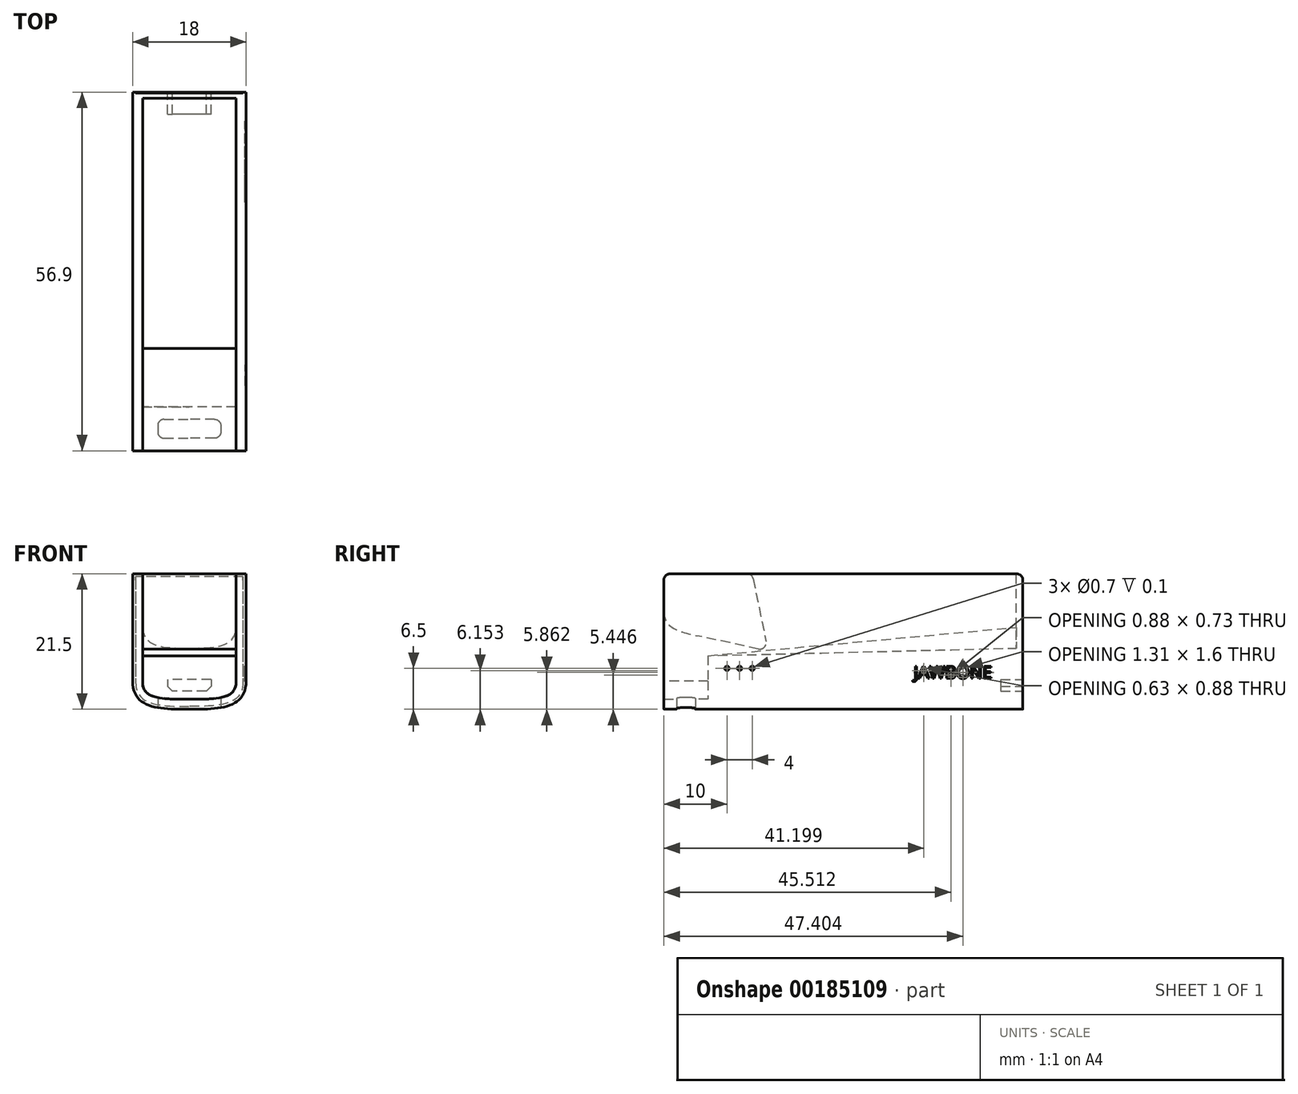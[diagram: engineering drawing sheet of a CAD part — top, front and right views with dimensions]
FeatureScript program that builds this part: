
annotation { "Feature Type Name" : "Feature", "Feature Type Description" : "" }
export const myFeature = defineFeature(function(context is Context, id is Id, definition is map)
    precondition{}
    {
        {
            var Q0;
            Q0=qCreatedBy(makeId("Front.planeOp"),FACE);
            var sketch = newSketch(context, id + "F0", { "sketchPlane" : qUnion([Q0])});
            skLineSegment(sketch, "E0", {"start": v(0, 21.5) * mm, "end": v(-9, 21.5) * mm});
            skLineSegment(sketch, "E1", {"start": v(-9, 21.5) * mm, "end": v(-9, 4.5) * mm});
            skFitSpline(sketch, "E2", {"points": [v(-9, 4.5) * mm, v(0, 0) * mm], "startDerivative": vector(0, -13.5) * mm, "endDerivative": vector(13.5, 0) * mm});
            skLineSegment(sketch, "E3", {"start": v(0, 21.5) * mm, "end": v(0, 0) * mm, "construction": true});
            skLineSegment(sketch, "E4.MirrorCS", {"start": v(0, 21.5) * mm, "end": v(9, 21.5) * mm});
            skLineSegment(sketch, "E5.MirrorCS", {"start": v(9, 21.5) * mm, "end": v(9, 4.5) * mm});
            skFitSpline(sketch, "E6.MirrorCS", {"points": [v(9, 4.5) * mm, v(0, 0) * mm], "startDerivative": vector(0, -13.5) * mm, "endDerivative": vector(-13.5, 0) * mm});
            skLineSegment(sketch, "E7", {"start": v(-9, 4.5) * mm, "end": v(-9, 0) * mm, "construction": true});
            skLineSegment(sketch, "E8", {"start": v(-9, 0) * mm, "end": v(-4.5, 0) * mm, "construction": true});
            skLineSegment(sketch, "E9", {"start": v(-4.5, 0) * mm, "end": v(0, 0) * mm, "construction": true});
            skSolve(sketch);
        }
        {
            var Q0;
            Q0=makeQuery(id+"F0.imprint","IMPRINT",FACE,{"disambiguationData":[TD([[makeQuery(id+"F0.imprint","IMPRINT",EDGE,{"derivedFrom":sQuery(id+"F0.wireOp",EDGE,"E0")}),1.0]])]});
            extrude(context, id + "F1", {"entities" : qUnion([Q0]), "depth" : 56.9 * mm});
        }
        {
            var Q0;
            Q0=makeQuery(id+"F1.opExtrude","SWEPT_BODY",BODY,{"disambiguationData":[OSD([sQuery(id+"F0.wireOp",EDGE,"E0"),sQuery(id+"F0.wireOp",EDGE,"E1"),sQuery(id+"F0.wireOp",EDGE,"E2"),sQuery(id+"F0.wireOp",EDGE,"E4.MirrorCS"),sQuery(id+"F0.wireOp",EDGE,"E5.MirrorCS"),sQuery(id+"F0.wireOp",EDGE,"E6.MirrorCS")])]});
            var Q1;
            Q1=sQuery(id+"F0.wireOp",EDGE,"E3");
            transform(context, id + "F2", {"entities" : qUnion([Q0]), "transformType" : TransformType.ROTATION, "transformAxis" : qUnion([Q1]), "angle" : 180 * degree, "makeCopy" : false});
        }
        {
            var Q0;
            Q0=makeQuery(id+"F1.opExtrude","CAP_FACE",FACE,{"disambiguationData":[OSD([sQuery(id+"F0.wireOp",EDGE,"E0"),sQuery(id+"F0.wireOp",EDGE,"E1"),sQuery(id+"F0.wireOp",EDGE,"E2"),sQuery(id+"F0.wireOp",EDGE,"E4.MirrorCS"),sQuery(id+"F0.wireOp",EDGE,"E5.MirrorCS"),sQuery(id+"F0.wireOp",EDGE,"E6.MirrorCS")])],"isStart":false});
            cPlane(context, id + "F3", {"entities" : qUnion([Q0]), "cplaneType" : CPlaneType.OFFSET, "offset" : 0 * mm, "width" : 150 * mm, "height" : 150 * mm});
        }
        {
            var Q0;
            Q0=qCreatedBy(id+"F3.planeOp",FACE);
            var sketch = newSketch(context, id + "F4", { "sketchPlane" : qUnion([Q0])});
            skLineSegment(sketch, "E10.0", {"start": v(8.5, 21.5) * mm, "end": v(8.5, 4.5) * mm});
            skFitSpline(sketch, "E10.1", {"points": [v(8.5, 4.5) * mm, v(8.5, 3.98) * mm, v(8.37, 3.1) * mm, v(7.88, 2.16) * mm, v(7.12, 1.49) * mm, v(6.07, 1) * mm, v(4.78, 0.7) * mm, v(2.8, 0.5) * mm, v(1.13, 0.5) * mm, v(0, 0.5) * mm]});
            skFitSpline(sketch, "E10.2", {"points": [v(-8.5, 4.5) * mm, v(-8.5, 3.98) * mm, v(-8.37, 3.1) * mm, v(-7.88, 2.16) * mm, v(-7.12, 1.49) * mm, v(-6.07, 1) * mm, v(-4.78, 0.7) * mm, v(-2.8, 0.5) * mm, v(-1.13, 0.5) * mm, v(0, 0.5) * mm]});
            skLineSegment(sketch, "E10.3", {"start": v(-8.5, 21.5) * mm, "end": v(-8.5, 4.5) * mm});
            skLineSegment(sketch, "E11", {"start": v(-8.5, 21.5) * mm, "end": v(8.5, 21.5) * mm});
            skSolve(sketch);
        }
        {
            var Q0;
            Q0 = qSketchRegion(id + "F4", true);
            extrude(context, id + "F5", {"entities" : qUnion([Q0]), "operationType" : NewBodyOperationType.REMOVE, "oppositeDirection" : true, "depth" : 0.15 * mm});
        }
        {
            var Q0;
            Q0=makeQuery(id+"F1.opExtrude","CAP_EDGE",EDGE,{"disambiguationData":[OSD([sQuery(id+"F0.wireOp",EDGE,"E0"),sQuery(id+"F0.wireOp",EDGE,"E4.MirrorCS")])],"isStart":false});
            var Q1;
            Q1=makeQuery(id+"F1.opExtrude","CAP_EDGE",EDGE,{"disambiguationData":[OSD([sQuery(id+"F0.wireOp",EDGE,"E0"),sQuery(id+"F0.wireOp",EDGE,"E4.MirrorCS")])],"isStart":true});
            fillet(context, id + "F6", {"entities" : qUnion([Q0, Q1]), "radius" : 1 * mm, "allowEdgeOverflow" : false});
        }
        {
            var Q0;
            Q0=makeQuery(id+"F1.opExtrude","CAP_FACE",FACE,{"disambiguationData":[OSD([sQuery(id+"F0.wireOp",EDGE,"E0"),sQuery(id+"F0.wireOp",EDGE,"E1"),sQuery(id+"F0.wireOp",EDGE,"E2"),sQuery(id+"F0.wireOp",EDGE,"E4.MirrorCS"),sQuery(id+"F0.wireOp",EDGE,"E5.MirrorCS"),sQuery(id+"F0.wireOp",EDGE,"E6.MirrorCS")])],"isStart":false});
            cPlane(context, id + "F7", {"entities" : qUnion([Q0]), "cplaneType" : CPlaneType.OFFSET, "offset" : 0 * mm, "width" : 150 * mm, "height" : 150 * mm});
        }
        {
            var Q0;
            Q0=qCreatedBy(id+"F7.planeOp",FACE);
            var sketch = newSketch(context, id + "F8", { "sketchPlane" : qUnion([Q0])});
            skLineSegment(sketch, "E12", {"start": v(0, 4.75) * mm, "end": v(-3.45, 4.75) * mm});
            skLineSegment(sketch, "E13", {"start": v(-3.45, 4.75) * mm, "end": v(-3.45, 3.65) * mm});
            skLineSegment(sketch, "E14", {"start": v(-3.45, 3.65) * mm, "end": v(-2.7, 2.9) * mm});
            skLineSegment(sketch, "E15", {"start": v(-2.7, 2.9) * mm, "end": v(0, 2.9) * mm});
            skLineSegment(sketch, "E16.MirrorCS", {"start": v(0, 4.75) * mm, "end": v(3.45, 4.75) * mm});
            skLineSegment(sketch, "E17.MirrorCS", {"start": v(3.45, 4.75) * mm, "end": v(3.45, 3.65) * mm});
            skLineSegment(sketch, "E18.MirrorCS", {"start": v(3.45, 3.65) * mm, "end": v(2.7, 2.9) * mm});
            skLineSegment(sketch, "E19.MirrorCS", {"start": v(2.7, 2.9) * mm, "end": v(0, 2.9) * mm});
            skSolve(sketch);
        }
        {
            var Q0;
            Q0 = qSketchRegion(id + "F8", true);
            extrude(context, id + "F9", {"entities" : qUnion([Q0]), "operationType" : NewBodyOperationType.REMOVE, "oppositeDirection" : true, "depth" : 3.5 * mm});
        }
        {
            var Q0;
            Q0=qCreatedBy(makeId("Front.planeOp"),FACE);
            var sketch = newSketch(context, id + "F10", { "sketchPlane" : qUnion([Q0])});
            skLineSegment(sketch, "E20.0", {"start": v(-7.4, 21.5) * mm, "end": v(-7.4, 4.5) * mm});
            skFitSpline(sketch, "E20.1", {"points": [v(-7.4, 4.5) * mm, v(-7.4, 4.07) * mm, v(-7.32, 3.57) * mm, v(-7.14, 3.13) * mm, v(-6.97, 2.87) * mm, v(-6.76, 2.65) * mm, v(-6.4, 2.37) * mm, v(-5.74, 2.06) * mm, v(-4.6, 1.8) * mm, v(-3.23, 1.65) * mm, v(-1.67, 1.6) * mm, v(-0.56, 1.6) * mm, v(0, 1.6) * mm]});
            skFitSpline(sketch, "E20.2", {"points": [v(7.4, 4.5) * mm, v(7.4, 4.07) * mm, v(7.32, 3.57) * mm, v(7.14, 3.13) * mm, v(6.97, 2.87) * mm, v(6.76, 2.65) * mm, v(6.4, 2.37) * mm, v(5.74, 2.06) * mm, v(4.6, 1.8) * mm, v(3.23, 1.65) * mm, v(1.67, 1.6) * mm, v(0.56, 1.6) * mm, v(0, 1.6) * mm]});
            skLineSegment(sketch, "E20.3", {"start": v(7.4, 21.5) * mm, "end": v(7.4, 4.5) * mm});
            skLineSegment(sketch, "E21", {"start": v(7.4, 21.5) * mm, "end": v(-7.4, 21.5) * mm});
            skSolve(sketch);
        }
        {
            var Q0;
            {var subQ1=sQuery(id+"F10.wireOp",EDGE,"E20.1");Q0=makeQuery(id+"F10.imprint","IMPRINT",FACE,{"disambiguationData":[TD([[makeQuery(id+"F10.imprint","IMPRINT",EDGE,{"derivedFrom":subQ1}),1.0]])]});}
            var Q1;
            {var subQ0=sQuery(id+"F10.wireOp",EDGE,"E21");Q1=makeQuery(id+"F10.imprint","IMPRINT",FACE,{"disambiguationData":[TD([[makeQuery(id+"F10.imprint","IMPRINT",EDGE,{"derivedFrom":subQ0}),1.0]])]});}
            extrude(context, id + "F11", {"entities" : qUnion([Q0, Q1]), "operationType" : NewBodyOperationType.REMOVE, "oppositeDirection" : true, "depth" : 7 * mm});
        }
        {
            var Q0;
            {var subQ0=sQuery(id+"F0.wireOp",EDGE,"E4.MirrorCS");var subQ1=sQuery(id+"F0.wireOp",EDGE,"E0");Q0=makeQuery(id+"F6.opFillet","BLEND_EDGE",EDGE,{"blendedFrom":[makeQuery(id+"F1.opExtrude","CAP_EDGE",EDGE,{"disambiguationData":[OSD([subQ1,subQ0])],"isStart":false}),makeQuery(id+"F1.opExtrude","SWEPT_FACE",FACE,{"disambiguationData":[OSD([subQ1,subQ0])]})],"blendedInto":[makeQuery(id+"F1.opExtrude","SWEPT_FACE",FACE,{"disambiguationData":[OSD([subQ1,subQ0])]})]});}
            cPoint(context, id + "F12", {"entities" : qUnion([Q0]), "parameter" : 0.5});
        }
        {
            var Q0;
            Q0=makeQuery(id+"F1.opExtrude","CAP_FACE",FACE,{"disambiguationData":[OSD([sQuery(id+"F0.wireOp",EDGE,"E0"),sQuery(id+"F0.wireOp",EDGE,"E1"),sQuery(id+"F0.wireOp",EDGE,"E2"),sQuery(id+"F0.wireOp",EDGE,"E4.MirrorCS"),sQuery(id+"F0.wireOp",EDGE,"E5.MirrorCS"),sQuery(id+"F0.wireOp",EDGE,"E6.MirrorCS")])],"isStart":false});
            var Q1;
            Q1 = qCreatedBy(id + "F12" ,VERTEX);
            cPlane(context, id + "F13", {"entities" : qUnion([Q0, Q1]), "cplaneType" : CPlaneType.PLANE_POINT, "offset" : 25 * mm, "width" : 150 * mm, "height" : 150 * mm});
        }
        {
            var Q0;
            Q0=makeQuery(id+"F11.boolean.opBoolean","COPY",FACE,{"derivedFrom":makeQuery(id+"F11.opExtrude","CAP_FACE",FACE,{"disambiguationData":[OSD([sQuery(id+"F10.wireOp",EDGE,"E20.0"),sQuery(id+"F10.wireOp",EDGE,"E20.1"),sQuery(id+"F10.wireOp",EDGE,"E20.2"),sQuery(id+"F10.wireOp",EDGE,"E20.3"),sQuery(id+"F10.wireOp",EDGE,"E21")])],"isStart":false})});
            cPlane(context, id + "F14", {"entities" : qUnion([Q0]), "cplaneType" : CPlaneType.OFFSET, "offset" : 0 * mm, "width" : 150 * mm, "height" : 150 * mm});
        }
        {
            var Q0;
            Q0=qCreatedBy(id+"F14.planeOp",FACE);
            var sketch = newSketch(context, id + "F15", { "sketchPlane" : qUnion([Q0])});
            skLineSegment(sketch, "E22", {"start": v(-7.4, 21.5) * mm, "end": v(7.4, 21.5) * mm});
            skLineSegment(sketch, "E23", {"start": v(-7.4, 21.5) * mm, "end": v(-7.4, 8.5) * mm});
            skLineSegment(sketch, "E24", {"start": v(7.4, 8.5) * mm, "end": v(-7.4, 8.5) * mm});
            skLineSegment(sketch, "E25", {"start": v(7.4, 8.5) * mm, "end": v(7.4, 21.5) * mm});
            skSolve(sketch);
        }
        {
            var Q0;
            Q0=qCreatedBy(id+"F13.planeOp",FACE);
            var sketch = newSketch(context, id + "F16", { "sketchPlane" : qUnion([Q0])});
            skLineSegment(sketch, "E26", {"start": v(-7.4, 21.5) * mm, "end": v(7.4, 21.5) * mm});
            skLineSegment(sketch, "E27", {"start": v(-7.4, 21.5) * mm, "end": v(-7.4, 13) * mm});
            skLineSegment(sketch, "E28", {"start": v(7.4, 13) * mm, "end": v(7.4, 21.5) * mm});
            skFitSpline(sketch, "E29", {"points": [v(7.4, 13) * mm, v(0, 9.7) * mm, v(-7.4, 13) * mm], "startDerivative": vector(0, -19.8) * mm, "endDerivative": vector(0, 19.8) * mm});
            skLineSegment(sketch, "E30", {"start": v(7.4, 13) * mm, "end": v(7.4, 9.7) * mm, "construction": true});
            skLineSegment(sketch, "E31", {"start": v(-7.4, 9.7) * mm, "end": v(0, 9.7) * mm, "construction": true});
            skLineSegment(sketch, "E32", {"start": v(0, 9.7) * mm, "end": v(7.4, 9.7) * mm, "construction": true});
            skLineSegment(sketch, "E33", {"start": v(-7.4, 9.7) * mm, "end": v(-7.4, 13) * mm, "construction": true});
            skSolve(sketch);
        }
        {
            var Q1;
            Q1 = qSketchRegion(id + "F15", true);
            var Q2;
            Q2 = qSketchRegion(id + "F16", true);
            loft(context, id + "F17", {"operationType" : NewBodyOperationType.REMOVE, "sheetProfilesArray" : [{ "sheetProfileEntities" : qUnion([Q1]) }, { "sheetProfileEntities" : qUnion([Q2]) }]});
        }
        {
            var Q0;
            {var subQ0=sQuery(id+"F0.wireOp",EDGE,"E4.MirrorCS");var subQ1=sQuery(id+"F0.wireOp",EDGE,"E0");Q0=makeQuery(id+"F17.boolean.opBoolean","SPLIT",FACE,{"disambiguationData":[TD([makeQuery(id+"F1.opExtrude","SWEPT_FACE",FACE,{"disambiguationData":[OSD([sQuery(id+"F0.wireOp",EDGE,"E1")])]})])],"derivedFrom":makeQuery(id+"F1.opExtrude","SWEPT_FACE",FACE,{"disambiguationData":[OSD([subQ1,subQ0])]})});}
            var Q1;
            Q1=qCreatedBy(makeId("Origin.pointOp"),VERTEX);
            cPlane(context, id + "F18", {"entities" : qUnion([Q0, Q1]), "cplaneType" : CPlaneType.PLANE_POINT, "offset" : 25 * mm, "width" : 150 * mm, "height" : 150 * mm});
        }
        {
            var Q0;
            Q0=qCreatedBy(id+"F18.planeOp",FACE);
            var sketch = newSketch(context, id + "F19", { "sketchPlane" : qUnion([Q0])});
            skLineSegment(sketch, "E34.top", {"start": v(-10.72, 0) * mm, "end": v(11.6, 0) * mm, "construction": true});
            skLineSegment(sketch, "E35.0", {"start": v(-4, 2) * mm, "end": v(4, 2) * mm});
            skLineSegment(sketch, "E35.1", {"start": v(-5, 3) * mm, "end": v(-5, 4) * mm});
            skLineSegment(sketch, "E35.2", {"start": v(-4, 5) * mm, "end": v(4, 5) * mm});
            skLineSegment(sketch, "E35.3", {"start": v(5, 3) * mm, "end": v(5, 4) * mm});
            skPoint(sketch, "E36.visualSharp", {"position": v(-5, 2) * mm});
            skArc(sketch, "E36.filletArc", {"start": v(-5, 3) * mm, "mid": v(-4.7, 2.3) * mm, "end": v(-4, 2) * mm});
            skPoint(sketch, "E37.visualSharp", {"position": v(5, 2) * mm});
            skArc(sketch, "E37.filletArc", {"start": v(4, 2) * mm, "mid": v(4.7, 2.3) * mm, "end": v(5, 3) * mm});
            skPoint(sketch, "E38.visualSharp", {"position": v(5, 5) * mm});
            skArc(sketch, "E38.filletArc", {"start": v(5, 4) * mm, "mid": v(4.7, 4.7) * mm, "end": v(4, 5) * mm});
            skPoint(sketch, "E39.visualSharp", {"position": v(-5, 5) * mm});
            skArc(sketch, "E39.filletArc", {"start": v(-4, 5) * mm, "mid": v(-4.7, 4.7) * mm, "end": v(-5, 4) * mm});
            skPoint(sketch, "E40", {"position": v(0, 2) * mm});
            skSolve(sketch);
        }
        {
            var Q0;
            Q0=makeQuery(id+"F19.imprint","IMPRINT",FACE,{"disambiguationData":[TD([[makeQuery(id+"F19.imprint","IMPRINT",EDGE,{"derivedFrom":sQuery(id+"F19.wireOp",EDGE,"E35.0")}),1.0]])]});
            extrude(context, id + "F20", {"entities" : qUnion([Q0]), "operationType" : NewBodyOperationType.REMOVE, "endBound" : BoundingType.THROUGH_ALL, "depth" : 25 * mm});
        }
        {
            var Q0;
            Q0=makeQuery(id+"F17.boolean.opBoolean","MERGE",FACE,{"derivedFrom":[makeQuery(id+"F11.boolean.opBoolean","COPY",FACE,{"derivedFrom":makeQuery(id+"F11.opExtrude","SWEPT_FACE",FACE,{"disambiguationData":[OSD([sQuery(id+"F10.wireOp",EDGE,"E20.3")])]})}),makeQuery(id+"F17.opLoft","SWEPT_FACE",FACE,{"disambiguationData":[OSD([sQuery(id+"F15.wireOp",EDGE,"E22"),sQuery(id+"F15.wireOp",EDGE,"E24"),sQuery(id+"F15.wireOp",EDGE,"E25"),sQuery(id+"F16.wireOp",EDGE,"E26"),sQuery(id+"F16.wireOp",EDGE,"E27"),sQuery(id+"F16.wireOp",EDGE,"E29")])]})]});
            var sketch = newSketch(context, id + "F21", { "sketchPlane" : qUnion([Q0])});
            skLineSegment(sketch, "E41", {"start": v(-1, 21.5) * mm, "end": v(-13.18, 21.5) * mm});
            skLineSegment(sketch, "E42", {"start": v(-14.16, 20.7) * mm, "end": v(-16.2, 10.75) * mm});
            skLineSegment(sketch, "E43", {"start": v(-15, 9.58) * mm, "end": v(-5.26, 11.68) * mm});
            skLineSegment(sketch, "E44", {"start": v(0, 15.5) * mm, "end": v(0, 20.5) * mm});
            skFitSpline(sketch, "E45", {"points": [v(0, 15.5) * mm, v(-5.26, 11.68) * mm], "startDerivative": vector(0, -8.07) * mm, "endDerivative": vector(-7.89, -1.7) * mm});
            skLineSegment(sketch, "E46", {"start": v(-2.63, 12.24) * mm, "end": v(-5.26, 11.68) * mm, "construction": true});
            skLineSegment(sketch, "E47", {"start": v(0, 15.5) * mm, "end": v(0, 12.81) * mm, "construction": true});
            skLineSegment(sketch, "E48", {"start": v(0, 12.81) * mm, "end": v(-2.63, 12.24) * mm, "construction": true});
            skPoint(sketch, "E49.visualSharp", {"position": v(0, 21.5) * mm});
            skArc(sketch, "E49.filletArc", {"start": v(0, 20.5) * mm, "mid": v(-0.3, 21.2) * mm, "end": v(-1, 21.5) * mm});
            skPoint(sketch, "E50.visualSharp", {"position": v(-14, 21.5) * mm});
            skArc(sketch, "E50.filletArc", {"start": v(-13.18, 21.5) * mm, "mid": v(-13.82, 21.27) * mm, "end": v(-14.16, 20.7) * mm});
            skPoint(sketch, "E51.visualSharp", {"position": v(-16.5, 9.25) * mm});
            skArc(sketch, "E51.filletArc", {"start": v(-16.2, 10.75) * mm, "mid": v(-15.92, 9.84) * mm, "end": v(-15, 9.58) * mm});
            skPoint(sketch, "E52", {"position": v(-6, 15.5) * mm});
            skLineSegment(sketch, "E53", {"start": v(0, 15.5) * mm, "end": v(-6, 15.5) * mm, "construction": true});
            skLineSegment(sketch, "E54", {"start": v(-6, 15.5) * mm, "end": v(-6, 21.5) * mm, "construction": true});
            skSolve(sketch);
        }
        {
            var Q0;
            Q0 = qSketchRegion(id + "F21", true);
            var Q1;
            Q1=makeQuery(id+"F17.boolean.opBoolean","MERGE",FACE,{"derivedFrom":[makeQuery(id+"F11.boolean.opBoolean","COPY",FACE,{"derivedFrom":makeQuery(id+"F11.opExtrude","SWEPT_FACE",FACE,{"disambiguationData":[OSD([sQuery(id+"F10.wireOp",EDGE,"E20.0")])]})}),makeQuery(id+"F17.opLoft","SWEPT_FACE",FACE,{"disambiguationData":[OSD([sQuery(id+"F15.wireOp",EDGE,"E22"),sQuery(id+"F15.wireOp",EDGE,"E23"),sQuery(id+"F15.wireOp",EDGE,"E24"),sQuery(id+"F16.wireOp",EDGE,"E26"),sQuery(id+"F16.wireOp",EDGE,"E28"),sQuery(id+"F16.wireOp",EDGE,"E29")])]})]});
            extrude(context, id + "F22", {"entities" : qUnion([Q0]), "endBound" : BoundingType.UP_TO_SURFACE, "endBoundEntityFace" : qUnion([Q1]), "depth" : 25 * mm});
        }
        {
            var Q0;
            Q0=makeQuery(id+"F1.opExtrude","SWEPT_FACE",FACE,{"disambiguationData":[OSD([sQuery(id+"F0.wireOp",EDGE,"E1")])]});
            cPlane(context, id + "F23", {"entities" : qUnion([Q0]), "cplaneType" : CPlaneType.OFFSET, "offset" : 0 * mm, "width" : 150 * mm, "height" : 150 * mm});
        }
        {
            var Q0;
            Q0=qCreatedBy(id+"F23.planeOp",FACE);
            var sketch = newSketch(context, id + "F24", { "sketchPlane" : qUnion([Q0])});
            skCircle(sketch, "E55", {"center": v(10, 6.5) * mm, "radius": 0.35 * mm});
            skCircle(sketch, "E56.1.0.0", {"center": v(12, 6.5) * mm, "radius": 0.35 * mm});
            skCircle(sketch, "E56.2.0.0", {"center": v(14, 6.5) * mm, "radius": 0.35 * mm});
            skLineSegment(sketch, "E56.direction1", {"start": v(10, 6.5) * mm, "end": v(12, 6.5) * mm, "construction": true});
            skSolve(sketch);
        }
        {
            var Q0;
            Q0 = qSketchRegion(id + "F24", true);
            var Q1;
            Q1 = qConstructionFilter(qBodyType(qCreatedBy(id + "F24" ,EDGE), BodyType.WIRE), ConstructionObject.NO);
            extrude(context, id + "F25", {"entities" : qUnion([Q0]), "surfaceEntities" : qUnion([Q1]), "oppositeDirection" : true, "depth" : 0.1 * mm});
        }
        {
            var Q0;
            Q0=makeQuery(id+"F25.opExtrude","SWEPT_BODY",BODY,{"disambiguationData":[OSD([sQuery(id+"F24.wireOp",EDGE,"E55")])]});
            var Q1;
            Q1=makeQuery(id+"F25.opExtrude","SWEPT_BODY",BODY,{"disambiguationData":[OSD([sQuery(id+"F24.wireOp",EDGE,"E56.1.0.0")])]});
            var Q2;
            Q2=makeQuery(id+"F25.opExtrude","SWEPT_BODY",BODY,{"disambiguationData":[OSD([sQuery(id+"F24.wireOp",EDGE,"E56.2.0.0")])]});
            var Q3;
            Q3=makeQuery(id+"F1.opExtrude","SWEPT_BODY",BODY,{"disambiguationData":[OSD([sQuery(id+"F0.wireOp",EDGE,"E0"),sQuery(id+"F0.wireOp",EDGE,"E1"),sQuery(id+"F0.wireOp",EDGE,"E2"),sQuery(id+"F0.wireOp",EDGE,"E4.MirrorCS"),sQuery(id+"F0.wireOp",EDGE,"E5.MirrorCS"),sQuery(id+"F0.wireOp",EDGE,"E6.MirrorCS")])]});
            booleanBodies(context, id + "F26", {"operationType" : BooleanOperationType.SUBTRACTION, "tools" : qUnion([Q0, Q1, Q2]), "targets" : qUnion([Q3]), "keepTools" : true});
        }
        {
            var Q0;
            Q0=qCreatedBy(id+"F23.planeOp",FACE);
            var sketch = newSketch(context, id + "F27", { "sketchPlane" : qUnion([Q0])});
            skLineSegment(sketch, "E57.bottom", {"start": v(10.35, 6.5) * mm, "end": v(13.65, 6.5) * mm});
            skLineSegment(sketch, "E57.top", {"start": v(10.35, 6.5) * mm, "end": v(13.65, 6.5) * mm});
            skLineSegment(sketch, "E57.left", {"start": v(10.35, 6.5) * mm, "end": v(10.35, 6.5) * mm});
            skLineSegment(sketch, "E57.right", {"start": v(13.65, 6.5) * mm, "end": v(13.65, 6.5) * mm});
            skSolve(sketch);
        }
        {
            var Q0;
            Q0 = qSketchRegion(id + "F27", true);
            extrude(context, id + "F28", {"entities" : qUnion([Q0]), "oppositeDirection" : true, "depth" : 0.1 * mm, "hasSecondDirection" : true, "secondDirectionOppositeDirection" : true, "secondDirectionDepth" : 0.05 * mm});
        }
        {
            var Q0;
            Q0=qCreatedBy(id+"F23.planeOp",FACE);
            var sketch = newSketch(context, id + "F29", { "sketchPlane" : qUnion([Q0])});
            skText(sketch, "E58", { "text": "JAWBONE", "fontName": "OpenSans-Regular.ttf"});
            skLineSegment(sketch, "E59", {"start": v(51.9, 9.16) * mm, "end": v(51.9, 4.02) * mm, "construction": true});
            skLineSegment(sketch, "E60", {"start": v(39.4, 9.11) * mm, "end": v(39.4, 3.98) * mm, "construction": true});
            const initialGuessF29  = {"E58": [0.03961, 0.00489, 1, 0, 0.00196]};
            skSetInitialGuess(sketch, initialGuessF29);
            skSolve(sketch);
        }
        {
            var Q0;
            Q0 = qSketchRegion(id + "F29", true);
            extrude(context, id + "F30", {"entities" : qUnion([Q0]), "oppositeDirection" : true, "depth" : 0.2 * mm});
        }
        {
            var Q0;
            Q0=qCreatedBy(id+"F23.planeOp",FACE);
            var sketch = newSketch(context, id + "F31", { "sketchPlane" : qUnion([Q0])});
            skLineSegment(sketch, "E61.bottom", {"start": v(39.61, 5.87) * mm, "end": v(52.3, 5.87) * mm});
            skLineSegment(sketch, "E61.top", {"start": v(39.61, 5.86) * mm, "end": v(52.3, 5.86) * mm});
            skLineSegment(sketch, "E61.left", {"start": v(39.61, 5.87) * mm, "end": v(39.61, 5.86) * mm});
            skLineSegment(sketch, "E61.right", {"start": v(52.3, 5.87) * mm, "end": v(52.3, 5.86) * mm});
            skSolve(sketch);
        }
        {
            var Q0;
            Q0 = qSketchRegion(id + "F31", true);
            extrude(context, id + "F32", {"entities" : qUnion([Q0]), "oppositeDirection" : true, "depth" : 0.2 * mm, "hasSecondDirection" : true, "secondDirectionOppositeDirection" : true, "secondDirectionDepth" : 0.1 * mm});
        }
        {
            var Q0;
            Q0=makeQuery(id+"F1.opExtrude","SWEPT_BODY",BODY,{"disambiguationData":[OSD([sQuery(id+"F0.wireOp",EDGE,"E0"),sQuery(id+"F0.wireOp",EDGE,"E1"),sQuery(id+"F0.wireOp",EDGE,"E2"),sQuery(id+"F0.wireOp",EDGE,"E4.MirrorCS"),sQuery(id+"F0.wireOp",EDGE,"E5.MirrorCS"),sQuery(id+"F0.wireOp",EDGE,"E6.MirrorCS")])]});
            var Q1;
            Q1=makeQuery(id+"F30.opExtrude","SWEPT_BODY",BODY,{"disambiguationData":[OSD([sQuery(id+"F29.wireOp",EDGE,"E58.sketch_text.stroke-0"),sQuery(id+"F29.wireOp",EDGE,"E58.sketch_text.stroke-1"),sQuery(id+"F29.wireOp",EDGE,"E58.sketch_text.stroke-2"),sQuery(id+"F29.wireOp",EDGE,"E58.sketch_text.stroke-3"),sQuery(id+"F29.wireOp",EDGE,"E58.sketch_text.stroke-4"),sQuery(id+"F29.wireOp",EDGE,"E58.sketch_text.stroke-5"),sQuery(id+"F29.wireOp",EDGE,"E58.sketch_text.stroke-6"),sQuery(id+"F29.wireOp",EDGE,"E58.sketch_text.stroke-7"),sQuery(id+"F29.wireOp",EDGE,"E58.sketch_text.stroke-8"),sQuery(id+"F29.wireOp",EDGE,"E58.sketch_text.stroke-9")])]});
            booleanBodies(context, id + "F33", {"operationType" : BooleanOperationType.INTERSECTION, "tools" : qUnion([Q0, Q1]), "keepTools" : true});
        }
        {
            var Q0;
            Q0=makeQuery(id+"F33.opBoolean","INTERSECT",BODY,{"derivedFrom":[makeQuery(id+"F1.opExtrude","SWEPT_BODY",BODY,{"disambiguationData":[OSD([sQuery(id+"F0.wireOp",EDGE,"E0"),sQuery(id+"F0.wireOp",EDGE,"E1"),sQuery(id+"F0.wireOp",EDGE,"E2"),sQuery(id+"F0.wireOp",EDGE,"E4.MirrorCS"),sQuery(id+"F0.wireOp",EDGE,"E5.MirrorCS"),sQuery(id+"F0.wireOp",EDGE,"E6.MirrorCS")])]}),makeQuery(id+"F30.opExtrude","SWEPT_BODY",BODY,{"disambiguationData":[OSD([sQuery(id+"F29.wireOp",EDGE,"E58.sketch_text.stroke-0"),sQuery(id+"F29.wireOp",EDGE,"E58.sketch_text.stroke-1"),sQuery(id+"F29.wireOp",EDGE,"E58.sketch_text.stroke-2"),sQuery(id+"F29.wireOp",EDGE,"E58.sketch_text.stroke-3"),sQuery(id+"F29.wireOp",EDGE,"E58.sketch_text.stroke-4"),sQuery(id+"F29.wireOp",EDGE,"E58.sketch_text.stroke-5"),sQuery(id+"F29.wireOp",EDGE,"E58.sketch_text.stroke-6"),sQuery(id+"F29.wireOp",EDGE,"E58.sketch_text.stroke-7"),sQuery(id+"F29.wireOp",EDGE,"E58.sketch_text.stroke-8"),sQuery(id+"F29.wireOp",EDGE,"E58.sketch_text.stroke-9")])]})]});
            var Q1;
            Q1=makeQuery(id+"F1.opExtrude","SWEPT_BODY",BODY,{"disambiguationData":[OSD([sQuery(id+"F0.wireOp",EDGE,"E0"),sQuery(id+"F0.wireOp",EDGE,"E1"),sQuery(id+"F0.wireOp",EDGE,"E2"),sQuery(id+"F0.wireOp",EDGE,"E4.MirrorCS"),sQuery(id+"F0.wireOp",EDGE,"E5.MirrorCS"),sQuery(id+"F0.wireOp",EDGE,"E6.MirrorCS")])]});
            booleanBodies(context, id + "F34", {"operationType" : BooleanOperationType.SUBTRACTION, "tools" : qUnion([Q0]), "targets" : qUnion([Q1]), "keepTools" : true});
        }
        {
            var Q0;
            Q0=makeQuery(id+"F30.opExtrude","SWEPT_BODY",BODY,{"disambiguationData":[OSD([sQuery(id+"F29.wireOp",EDGE,"E58.sketch_text.stroke-0"),sQuery(id+"F29.wireOp",EDGE,"E58.sketch_text.stroke-1"),sQuery(id+"F29.wireOp",EDGE,"E58.sketch_text.stroke-2"),sQuery(id+"F29.wireOp",EDGE,"E58.sketch_text.stroke-3"),sQuery(id+"F29.wireOp",EDGE,"E58.sketch_text.stroke-4"),sQuery(id+"F29.wireOp",EDGE,"E58.sketch_text.stroke-5"),sQuery(id+"F29.wireOp",EDGE,"E58.sketch_text.stroke-6"),sQuery(id+"F29.wireOp",EDGE,"E58.sketch_text.stroke-7"),sQuery(id+"F29.wireOp",EDGE,"E58.sketch_text.stroke-8"),sQuery(id+"F29.wireOp",EDGE,"E58.sketch_text.stroke-9")])]});
            deleteBodies(context, id + "F35", {"entities" : qUnion([Q0])});
        }
    });
